# Revit family: QF_BOURGEAT_Satellite4G_froid_1-1_entree530_pleine
name_source: partatom
category: Equipement spécialisé
revit_build: Autodesk Revit 2015 (Build: 20140606_1530(x64)
units: mm (PartAtom-declared; Revit-internal decimal feet)

## types (6) — shared parameters
Certification = NF hygiene alimentaire
Classe Climatique = 4
Diametre_roue = 160 mm  [stored 0.524934 ft]
Fabricant = BOURGEAT
Fréquence = 50 Hz
Hauteur_roue = 200 mm  [stored 0.656168 ft]
Indice de protection = IP25
Largeur_porte = 706 mm  [stored 2.31627 ft]
Longueur hors tout = 791 mm
Longueur_poignees_laterales = 648 mm  [stored 2.12598 ft]
Materiau_Poignee_porte = B_Elastomère_TPE_S
Materiau_bac = B_Elastomère_TPE_S
Materiau_bandage = B_Elastomère_TPE_S
Materiau_porte = Acier inoxydable, brossé
Materiau_vitre = Verre, vitrage transparent, trempé
Nature isolant = Mousse sans PU
Phase = 2
Pos_V_IHM = 38 mm  [stored 0.124672 ft]
Profondeur hors tout = 804 mm  [stored 2.6378 ft]
Spécification du Fabricant = Satellite 4G
Tension = 230 V
Type Fluide Frigorigène = R134a
URL catalogue = http://www.bourgeat.fr

## per-type parameters (varying)
| type | Charge max | Consommation énergétique | Hauteur hors tout | Hauteur_poignee_porte_sol | Hauteur_poignees_laterales | Hauteur_porte | Intensité nominale | Modèle | Poids net à vide | Poignee_droite | Poignee_gauche | Puissance frigorifique | Puissance électrique  |
| GN10_porte_inox_tirant_droit | 100.00 kg | 3Kwh/h NFD40-016 | 1123 mm  [stored 3.68438 ft] | 426 mm  [stored 1.39764 ft] | 804 mm  [stored 2.6378 ft] | 876 mm  [stored 2.87402 ft] | 1 A | 842010 + 844000 | 100.00 kg | Oui | Non | 270 W à -5°C | 300 W |
| GN15_porte_inox_tirant_droit | 150.00 kg | 3.4Kwh/h NFD40-016 | 1478 mm  [stored 4.84908 ft] | 513 mm  [stored 1.68307 ft] | 937 mm  [stored 3.07415 ft] | 1231 mm  [stored 4.03871 ft] | 1 A | 842015 + 844000 | 120.00 kg | Oui | Non | 270 W à -5°C | 300 W |
| GN20_porte_inox_tirant_droit | 200.00 kg | 3.8Kwh/h NFD40-016 | 1833 mm  [stored 6.01378 ft] | 768 mm  [stored 2.51969 ft] | 935 mm | 1586 mm  [stored 5.20341 ft] | 2 A | 842021 + 844000 | 140.00 kg | Oui | Non | 465 W à -5°C | 500 W |
| GN10_porte_inox_tirant_gauche | 100.00 kg | 3Kwh/h NFD40-016 | 1123 mm  [stored 3.68438 ft] | 426 mm  [stored 1.39764 ft] | 804 mm  [stored 2.6378 ft] | 876 mm  [stored 2.87402 ft] | 1 A | 842010 | 100.00 kg | Non | Oui | 270 W à -5°C | 300 W |
| GN15_porte_inox_tirant_gauche | 150.00 kg | 3.4Kwh/h NFD40-016 | 1478 mm  [stored 4.84908 ft] | 513 mm  [stored 1.68307 ft] | 937 mm  [stored 3.07415 ft] | 1231 mm  [stored 4.03871 ft] | 1 A | 842015 | 120.00 kg | Non | Oui | 270 W à -5°C | 300 W |
| GN20_porte_inox_tirant_gauche | 200.00 kg | 3.8Kwh/h NFD40-016 | 1833 mm  [stored 6.01378 ft] | 768 mm  [stored 2.51969 ft] | 935 mm | 1586 mm  [stored 5.20341 ft] | 2 A | 842021 | 140.00 kg | Non | Oui | 465 W à -5°C | 500 W |

note: [stored X ft] marks values corroborated as IEEE doubles in the binary element streams (Revit-internal decimal feet)
